# Revit family: Skyroofs_Kalwall_Pre-Engineered-SSRR-Hip-Ends
name_source: partatom
category: Windows
units: mm (PartAtom-declared; Revit-internal decimal feet)

## family parameters
Cut with Voids When Loaded = No
Host = Face
OmniClass Number = 23.25.20.14.27.17
OmniClass Title = Translucent Roof Assemblies
Room Calculation Point = No
Shared = No

## types (3) — shared parameters
Analytic Construction = <None>
Default Elevation = 4' - 0"
Define Thermal Properties by = Schematic Type
Description = Flat or curved, these systems span up to 24', offering the ultimate in energy-efficient diffuse daylighting.
Manufacturer = Kalwall
Model = Pre-engineered skyroof with Hip Ends
Product Documentation Link = https://www.kalwall.com
Product Page URL = https://www.kalwall.com
Product data url = https://bimobject.com
URL = https://www.kalwall.com
Version = 1

## type names
- Shoji 8" x 20"
- Shoji 10" x 24"
- Shoji 12" x 24"
type visibility flags: 3 boolean params named "<type name>" — each type sets only its own to Yes (folded from table)

## geometry (parser evidence)
native form markers: Sweep x27
no freeform markers — native parametric forms only
